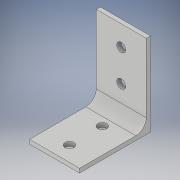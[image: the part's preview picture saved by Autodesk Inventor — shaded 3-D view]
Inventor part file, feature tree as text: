
AUTODESK INVENTOR PART (.ipt)
format: ipt  version: 2019 (Build 230136000, 136)  size: 142,848 bytes
history: native  units: in
note: dims shown in document units (in); Inventor stores cm internally (conversion verified against a paired STEP export)
features: extrude x4, sketch x4, fillet x1
ambient origin geometry x8: Origin, YZ Plane, XZ Plane, XY Plane, X Axis, Y Axis, Z Axis, Center Point
bodies: Solid1 (feature_tree)
feature tree (9):
  extrude  "Extrusion1"  Depth=0.6in
  extrude  "Extrusion2"  Depth=0.05in
  extrude  "Extrusion3"  Depth=0.8in
  fillet  "Fillet1"  Radius=0.107in
  sketch  "Sketch1"  dims[d0=1.0in d1=0.6in]
  sketch  "Sketch2"  dims[d2=0.05in d3=0.0in d4=0.05in]
  sketch  "Sketch3"  dims[d5=0.8in d6=0.0in d7=0.107in d8=0.107in]
  sketch  "Sketch4"  dims[d10=0.3in d11=0.379in d13=1.0in d14=0.0in d15=0.107in d17=0.394in d19=0.107in d22=0.0in d23=1.0in d24=0.125in d25=0.377in d26=0.3in d27=0.3in d28=0.3in]
  extrude  "Extrusion4"  Depth=0.125in
